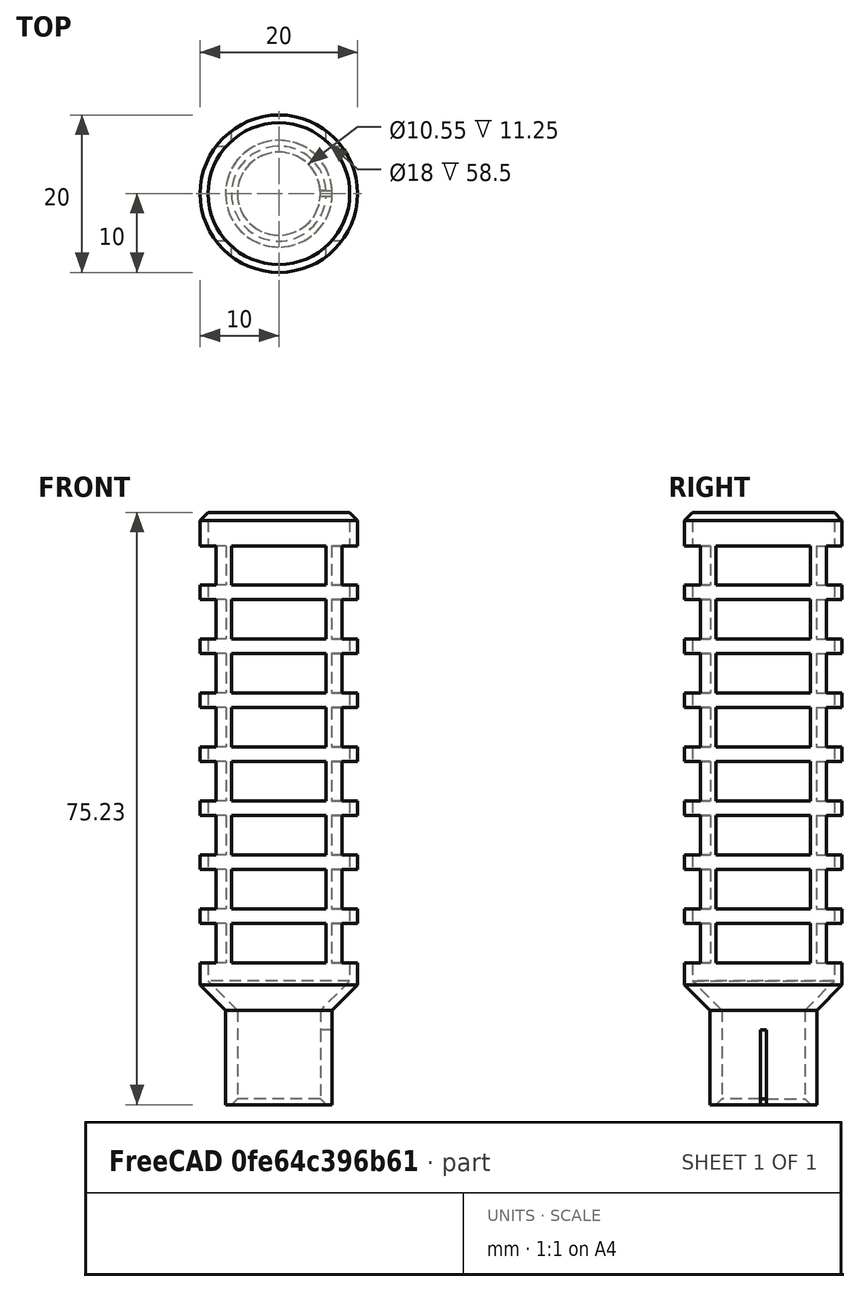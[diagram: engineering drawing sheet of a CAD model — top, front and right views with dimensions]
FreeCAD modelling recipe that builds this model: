
FCSTD DOCUMENT  (FreeCAD 0.21R33771 (Git))
Label: air-input-filter
License: All rights reserved
LicenseURL: https://en.wikipedia.org/wiki/All_rights_reserved
objects: Sketcher::SketchObject×4, PartDesign::Pocket×3, PartDesign::LinearPattern×2, PartDesign::Chamfer×2, PartDesign::Revolution×1, PartDesign::Body×1, App::Part×1, Mesh::Feature×1
note: 19 computed .brp shape members not serialized (recipe doc carries the construction recipe); baked Part::Feature solids carry a one-line shape summary decoded from their .brp

FEATURE [Sketcher::SketchObject] Sketch
  FullyConstrained = true
  MapMode = 5
  Placement = pos=(0,0,0) rot=(1,0,0;1.5708rad)
  Support = -> [XZ_Plane001]
  sketch-geometry (10):
    g0: LineSegment StartX=5.275 StartY=0 StartZ=0 EndX=5.275 EndY=-12 EndZ=0
    g1: LineSegment StartX=5.275 StartY=-12 StartZ=0 EndX=6.775 EndY=-12 EndZ=0
    g2: LineSegment StartX=6.775 StartY=-12 StartZ=0 EndX=6.775 EndY=0 EndZ=0
    g3: LineSegment StartX=6.775 StartY=0 StartZ=0 EndX=10 EndY=3.225 EndZ=0
    g4: LineSegment StartX=10 StartY=3.225 StartZ=0 EndX=10 EndY=63.225 EndZ=0
    g5: LineSegment StartX=9 StartY=62.225 StartZ=0 EndX=9 EndY=3.725 EndZ=0
    g6: LineSegment StartX=9 StartY=3.725 StartZ=0 EndX=5.275 EndY=0 EndZ=0
    g7: LineSegment StartX=0 StartY=63.225 StartZ=0 EndX=0 EndY=62.225 EndZ=0
    g8: LineSegment StartX=0 StartY=62.225 StartZ=0 EndX=9 EndY=62.225 EndZ=0
    g9: LineSegment StartX=0 StartY=63.225 StartZ=0 EndX=10 EndY=63.225 EndZ=0
  constraints (30):
    c: Vertical(g0)
    c: Coincident(g1,g0)
    c: Horizontal(g1)
    c: Coincident(g2,g1)
    c: Vertical(g2)
    c: Horizontal(g2,g0)
    c: DistanceY(g2,g2) = 12
    c: DistanceX(g-1,g0) = 5.275
    c: PointOnObject(g0,g-1)
    c: Coincident(g3,g2)
    c: Coincident(g4,g3)
    c: Vertical(g4)
    c: DistanceY(g4,g4) = 60
    c: DistanceX(g-1,g4) = 10
    c: Angle(g2,g3) = 2.35619
    c: Vertical(g5)
    c: Coincident(g6,g5)
    c: Coincident(g6,g0)
    c: Angle(g0,g6) = 2.35619
    c: Coincident(g8,g7)
    c: Horizontal(g8)
    c: Vertical(g7)
    c: PointOnObject(g7,g-2)
    c: Distance(g7) = 1
    c: Coincident(g5,g8)
    c: DistanceX(g5,g4) = 1
    c: Coincident(g9,g7)
    c: Coincident(g9,g4)
    c: Horizontal(g9)
    c: Distance(g1) = 1.5
FEATURE [PartDesign::Revolution] Revolution
  Angle = 360
  Axis = (0,2e-16,1)
  Base = (0,0,0)
  Placement = pos=(0,0,0) rot=(1,0,0;1.5708rad)
  Profile = -> Sketch
  ReferenceAxis = -> Sketch [V_Axis]
  Reversed = true
FEATURE [Sketcher::SketchObject] Sketch001
  AttachmentOffset = pos=(0,0,-2.5) rot=(0,0,1;0rad)
  FullyConstrained = true
  MapMode = 5
  Placement = pos=(0,0,-2.5) rot=(0,0,1;0rad)
  Support = -> [XY_Plane001]
  sketch-geometry (4):
    g0: LineSegment StartX=0 StartY=0.4 StartZ=0 EndX=30 EndY=0.4 EndZ=0
    g1: LineSegment StartX=30 StartY=0.4 StartZ=0 EndX=30 EndY=-0.4 EndZ=0
    g2: LineSegment StartX=30 StartY=-0.4 StartZ=0 EndX=0 EndY=-0.4 EndZ=0
    g3: LineSegment StartX=0 StartY=-0.4 StartZ=0 EndX=0 EndY=0.4 EndZ=0
  constraints (11):
    c: Coincident(g0,g1)
    c: Coincident(g1,g2)
    c: Coincident(g2,g3)
    c: Coincident(g3,g0)
    c: Horizontal(g0)
    c: Horizontal(g2)
    c: Vertical(g3)
    c: PointOnObject(g0,g-2)
    c: Symmetric(g0,g1,g-1)
    c: Distance(g2) = 30
    c: DistanceY(g1,g1) = 0.8
FEATURE [PartDesign::Pocket] Pocket
  BaseFeature = -> Revolution
  Direction = (0,0,-1)
  Length = 5
  Length2 = 5
  Placement = pos=(0,0,0) rot=(1,0,0;1.5708rad)
  Profile = -> Sketch001
  ReferenceAxis = -> Sketch001 [N_Axis]
  Type = 1
FEATURE [Sketcher::SketchObject] Sketch002
  FullyConstrained = true
  MapMode = 5
  Placement = pos=(0,0,0) rot=(1,0,0;1.5708rad)
  Support = -> [XZ_Plane001]
  sketch-geometry (4):
    g0: LineSegment StartX=-6 StartY=11 StartZ=0 EndX=6 EndY=11 EndZ=0
    g1: LineSegment StartX=6 StartY=11 StartZ=0 EndX=6 EndY=6 EndZ=0
    g2: LineSegment StartX=6 StartY=6 StartZ=0 EndX=-6 EndY=6 EndZ=0
    g3: LineSegment StartX=-6 StartY=6 StartZ=0 EndX=-6 EndY=11 EndZ=0
  constraints (11):
    c: Coincident(g0,g1)
    c: Coincident(g1,g2)
    c: Coincident(g2,g3)
    c: Coincident(g3,g0)
    c: Symmetric(g0,g0,g-2)
    c: Vertical(g3)
    c: Vertical(g1)
    c: Distance(g1) = 5
    c: Horizontal(g2)
    c: Distance(g0) = 12
    c: DistanceY(g-1,g1) = 6
FEATURE [PartDesign::Pocket] Pocket001
  BaseFeature = -> Pocket
  Direction = (0,1,-2e-16)
  Length = 5
  Length2 = 5
  Midplane = true
  Placement = pos=(0,0,0) rot=(1,0,0;1.5708rad)
  Profile = -> Sketch002
  ReferenceAxis = -> Sketch002 [N_Axis]
  Type = 1
FEATURE [PartDesign::LinearPattern] LinearPattern
  BaseFeature = -> Pocket001
  Direction = -> Sketch002 [V_Axis]
  Length = 48
  Occurrences = 8
  Originals = -> [Pocket001]
  Placement = pos=(0,0,0) rot=(1,0,0;1.5708rad)
FEATURE [Sketcher::SketchObject] Sketch003
  FullyConstrained = true
  MapMode = 5
  Placement = pos=(0,0,0) rot=(0.57735,0.57735,0.57735;2.0944rad)
  Support = -> [YZ_Plane001]
  sketch-geometry (4):
    g0: LineSegment StartX=-6 StartY=11 StartZ=0 EndX=6 EndY=11 EndZ=0
    g1: LineSegment StartX=6 StartY=11 StartZ=0 EndX=6 EndY=6 EndZ=0
    g2: LineSegment StartX=6 StartY=6 StartZ=0 EndX=-6 EndY=6 EndZ=0
    g3: LineSegment StartX=-6 StartY=6 StartZ=0 EndX=-6 EndY=11 EndZ=0
  constraints (11):
    c: Coincident(g0,g1)
    c: Coincident(g1,g2)
    c: Coincident(g2,g3)
    c: Coincident(g3,g0)
    c: Horizontal(g2)
    c: Vertical(g1)
    c: Vertical(g3)
    c: Symmetric(g0,g0,g-2)
    c: Distance(g1) = 5
    c: Distance(g0) = 12
    c: DistanceY(g-1,g1) = 6
FEATURE [PartDesign::Pocket] Pocket002
  BaseFeature = -> LinearPattern
  Direction = (-1,2e-16,-3e-16)
  Length = 5
  Length2 = 5
  Midplane = true
  Placement = pos=(0,0,0) rot=(1,0,0;1.5708rad)
  Profile = -> Sketch003
  ReferenceAxis = -> Sketch003 [N_Axis]
  Type = 1
FEATURE [PartDesign::LinearPattern] LinearPattern001
  BaseFeature = -> Pocket002
  Direction = -> Sketch003 [V_Axis]
  Length = 48
  Occurrences = 8
  Originals = -> [Pocket002]
  Placement = pos=(0,0,0) rot=(1,0,0;1.5708rad)
  expr: Length = <<LinearPattern>>.Length
  expr: Occurrences = <<LinearPattern>>.Occurrences
FEATURE [PartDesign::Chamfer] Chamfer
  Angle = 45
  Base = -> LinearPattern001 [Edge440]
  BaseFeature = -> LinearPattern001
  ChamferType = 0
  FlipDirection = false
  Placement = pos=(0,0,0) rot=(1,0,0;1.5708rad)
  Size = 1
  Size2 = 1
  SupportTransform = false
  UseAllEdges = false
FEATURE [PartDesign::Chamfer] Chamfer001
  Angle = 45
  Base = -> Chamfer [Edge459]
  BaseFeature = -> Chamfer
  ChamferType = 0
  FlipDirection = false
  Placement = pos=(0,0,0) rot=(1,0,0;1.5708rad)
  Size = 0.75
  Size2 = 1
  SupportTransform = false
  UseAllEdges = false
FEATURE [PartDesign::Body] Body
  Group = -> [Sketch,Revolution,Sketch001,Pocket,Sketch002,Pocket001,LinearPattern,Sketch003,Pocket002,LinearPattern001,Chamfer,Chamfer001]
  Origin = -> Origin001
  Tip = -> Chamfer001
FEATURE [App::Part] Part
  Group = -> [Body]
  Origin = -> Origin
FEATURE [Mesh::Feature] Mesh  label="Part (Meshed)"
  Placement = pos=(32,0,0) rot=(0,0,1;0rad)
